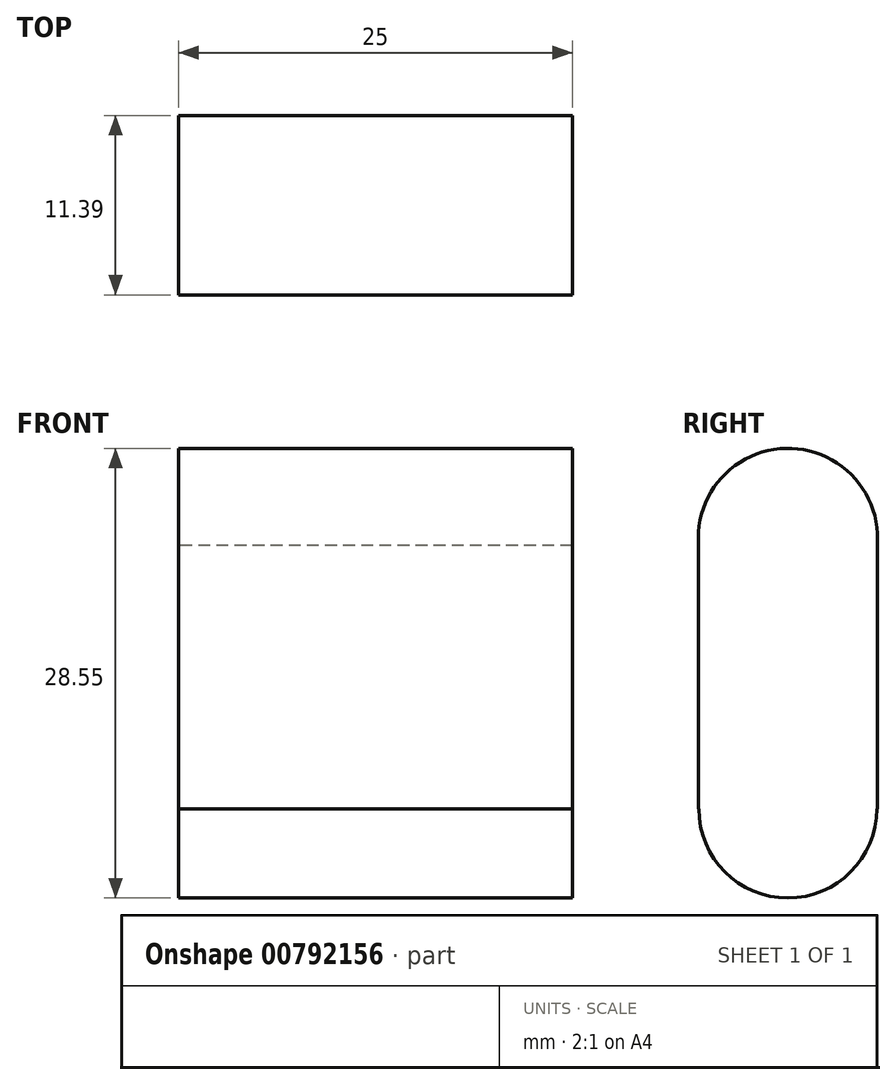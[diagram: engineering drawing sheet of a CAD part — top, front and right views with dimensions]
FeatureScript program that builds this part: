
annotation { "Feature Type Name" : "Feature", "Feature Type Description" : "" }
export const myFeature = defineFeature(function(context is Context, id is Id, definition is map)
    precondition{}
    {
        {
            var Q0;
            Q0=qCreatedBy(makeId("Top.planeOp"),FACE);
            var sketch = newSketch(context, id + "F0", { "sketchPlane" : qUnion([Q0])});
            skCircle(sketch, "E0", {"center": v(0, 0) * mm, "radius": 28.06 * mm});
            skCircle(sketch, "E1", {"center": v(0, 0) * mm, "radius": 26.28 * mm});
            skSolve(sketch);
        }
        {
            var Q0;
            Q0=sQuery(id+"F0.wireOp",EDGE,"E0");
            extrude(context, id + "F1", {"bodyType" : ToolBodyType.SURFACE, "surfaceEntities" : qUnion([Q0]), "depth" : 110 * mm, "offsetDistance" : 25 * mm});
        }
        {
            var Q0;
            Q0=qCreatedBy(makeId("Right.planeOp"),FACE);
            var sketch = newSketch(context, id + "F2", { "sketchPlane" : qUnion([Q0])});
            skCircle(sketch, "E2", {"center": v(-62.1, 63.27) * mm, "radius": 5.7 * mm});
            skLineSegment(sketch, "E3.bottom", {"start": v(-67.8, 63.27) * mm, "end": v(-56.42, 63.27) * mm});
            skLineSegment(sketch, "E3.top", {"start": v(-67.8, 46.05) * mm, "end": v(-56.42, 46.05) * mm});
            skLineSegment(sketch, "E3.left", {"start": v(-67.8, 63.27) * mm, "end": v(-67.8, 46.05) * mm});
            skLineSegment(sketch, "E3.right", {"start": v(-56.42, 63.27) * mm, "end": v(-56.42, 46.05) * mm});
            skCircle(sketch, "E4", {"center": v(-62.11, 46.05) * mm, "radius": 5.65 * mm});
            skSolve(sketch);
        }
        {
            var Q0;
            {var subQ0=sQuery(id+"F2.wireOp",EDGE,"E3.bottom");Q0=makeQuery(id+"F2.imprint","IMPRINT",FACE,{"disambiguationData":[TD([[makeQuery(id+"F2.imprint","IMPRINT",EDGE,{"derivedFrom":subQ0}),1.0]])]});}
            var Q1;
            {var subQ0=sQuery(id+"F2.wireOp",EDGE,"E4");var subQ1=sQuery(id+"F2.wireOp",EDGE,"E3.top");var subQ2=makeQuery(id+"F2.imprint","INTERSECT",VERTEX,{"disambiguationData":[OD(0.0)],"derivedFrom":[subQ1,subQ0]});Q1=makeQuery(id+"F2.imprint","IMPRINT",FACE,{"disambiguationData":[TD([[makeQuery(id+"F2.imprint","IMPRINT",EDGE,{"disambiguationData":[TD([[subQ2,-1.0]])],"derivedFrom":subQ1}),-1.0]])]});}
            var Q2;
            {var subQ0=sQuery(id+"F2.wireOp",EDGE,"E3.bottom");Q2=makeQuery(id+"F2.imprint","IMPRINT",FACE,{"disambiguationData":[TD([[makeQuery(id+"F2.imprint","IMPRINT",EDGE,{"derivedFrom":subQ0}),-1.0]])]});}
            var Q3;
            {var subQ0=sQuery(id+"F2.wireOp",EDGE,"E3.left");Q3=makeQuery(id+"F2.imprint","IMPRINT",FACE,{"disambiguationData":[TD([[makeQuery(id+"F2.imprint","IMPRINT",EDGE,{"derivedFrom":subQ0}),1.0]])]});}
            var Q4;
            {var subQ0=sQuery(id+"F2.wireOp",EDGE,"E4");var subQ1=sQuery(id+"F2.wireOp",EDGE,"E3.top");var subQ2=makeQuery(id+"F2.imprint","INTERSECT",VERTEX,{"disambiguationData":[OD(0.0)],"derivedFrom":[subQ1,subQ0]});Q4=makeQuery(id+"F2.imprint","IMPRINT",FACE,{"disambiguationData":[TD([[makeQuery(id+"F2.imprint","IMPRINT",EDGE,{"disambiguationData":[TD([[subQ2,-1.0]])],"derivedFrom":subQ1}),1.0]])]});}
            extrude(context, id + "F3", {"entities" : qUnion([Q0, Q1, Q2, Q3, Q4]), "depth" : 25 * mm, "offsetDistance" : 25 * mm});
        }
    });
